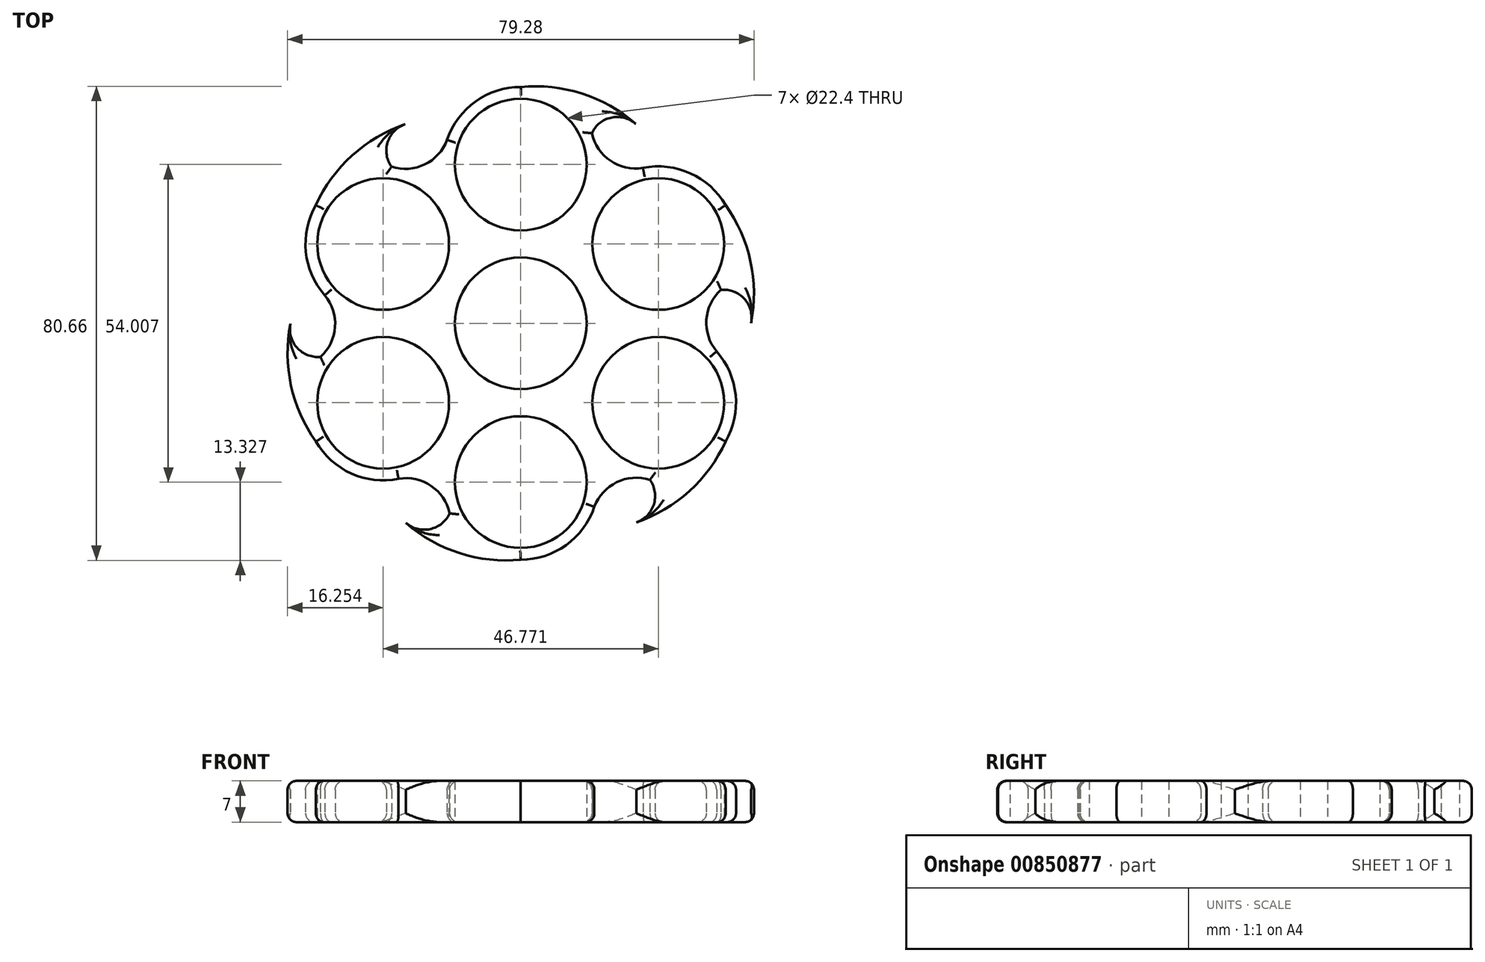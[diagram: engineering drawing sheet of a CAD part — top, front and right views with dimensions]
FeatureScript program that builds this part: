
annotation { "Feature Type Name" : "Feature", "Feature Type Description" : "" }
export const myFeature = defineFeature(function(context is Context, id is Id, definition is map)
    precondition{}
    {
        {
            var Q0;
            Q0=qCreatedBy(makeId("Top.planeOp"),FACE);
            var sketch = newSketch(context, id + "F0", { "sketchPlane" : qUnion([Q0])});
            skCircle(sketch, "E0", {"center": v(0, 0) * mm, "radius": 11.2 * mm});
            skCircle(sketch, "E1", {"center": v(0, 27) * mm, "radius": 11.2 * mm});
            skArc(sketch, "E2", {"start": v(12.73, 30.5) * mm, "mid": v(12.44, 31.42) * mm, "end": v(12.08, 32.33) * mm});
            skArc(sketch, "E3.1.0", {"start": v(-20.05, 26.27) * mm, "mid": v(-21, 26.48) * mm, "end": v(-21.96, 26.62) * mm});
            skCircle(sketch, "E3.1.1", {"center": v(-23.39, 13.5) * mm, "radius": 11.2 * mm});
            skArc(sketch, "E3.2.0", {"start": v(-32.78, -4.22) * mm, "mid": v(-33.43, -4.94) * mm, "end": v(-34.04, -5.7) * mm});
            skCircle(sketch, "E3.2.1", {"center": v(-23.39, -13.5) * mm, "radius": 11.2 * mm});
            skArc(sketch, "E3.3.0", {"start": v(-12.73, -30.5) * mm, "mid": v(-12.44, -31.42) * mm, "end": v(-12.08, -32.33) * mm});
            skCircle(sketch, "E3.3.1", {"center": v(0, -27) * mm, "radius": 11.2 * mm});
            skArc(sketch, "E3.4.0", {"start": v(20.05, -26.27) * mm, "mid": v(21, -26.48) * mm, "end": v(21.96, -26.62) * mm});
            skCircle(sketch, "E3.4.1", {"center": v(23.39, -13.5) * mm, "radius": 11.2 * mm});
            skArc(sketch, "E3.5.0", {"start": v(32.78, 4.22) * mm, "mid": v(33.43, 4.94) * mm, "end": v(34.04, 5.7) * mm});
            skCircle(sketch, "E3.5.1", {"center": v(23.39, 13.5) * mm, "radius": 11.2 * mm});
            skArc(sketch, "E4", {"start": v(12.08, 32.33) * mm, "mid": v(15.25, 27.64) * mm, "end": v(20.77, 26.44) * mm});
            skArc(sketch, "E5.1.0", {"start": v(-21.96, 26.62) * mm, "mid": v(-16.32, 27.02) * mm, "end": v(-12.51, 31.21) * mm});
            skArc(sketch, "E5.2.0", {"start": v(-34.04, -5.7) * mm, "mid": v(-31.56, -0.62) * mm, "end": v(-33.29, 4.77) * mm});
            skArc(sketch, "E5.3.0", {"start": v(-12.08, -32.33) * mm, "mid": v(-15.25, -27.64) * mm, "end": v(-20.77, -26.44) * mm});
            skArc(sketch, "E5.4.0", {"start": v(21.96, -26.62) * mm, "mid": v(16.32, -27.02) * mm, "end": v(12.51, -31.21) * mm});
            skArc(sketch, "E5.5.0", {"start": v(34.04, 5.7) * mm, "mid": v(31.56, 0.62) * mm, "end": v(33.29, -4.77) * mm});
            skArc(sketch, "E6", {"start": v(19.5, 33.94) * mm, "mid": v(10.4, 39.09) * mm, "end": v(0, 40.2) * mm});
            skArc(sketch, "E7", {"start": v(19.5, 33.94) * mm, "mid": v(15.4, 35) * mm, "end": v(12.08, 32.33) * mm});
            skArc(sketch, "E8.1.0", {"start": v(-19.64, 33.87) * mm, "mid": v(-28.65, 28.55) * mm, "end": v(-34.82, 20.1) * mm});
            skArc(sketch, "E8.1.1", {"start": v(-19.64, 33.87) * mm, "mid": v(-22.61, 30.83) * mm, "end": v(-21.96, 26.62) * mm});
            skArc(sketch, "E8.2.0", {"start": v(-39.15, -0.07) * mm, "mid": v(-39.05, -10.54) * mm, "end": v(-34.82, -20.1) * mm});
            skArc(sketch, "E8.2.1", {"start": v(-39.15, -0.07) * mm, "mid": v(-38, -4.17) * mm, "end": v(-34.04, -5.7) * mm});
            skArc(sketch, "E8.3.0", {"start": v(-19.5, -33.94) * mm, "mid": v(-10.4, -39.09) * mm, "end": v(0, -40.2) * mm});
            skArc(sketch, "E8.3.1", {"start": v(-19.5, -33.94) * mm, "mid": v(-15.4, -35) * mm, "end": v(-12.08, -32.33) * mm});
            skArc(sketch, "E8.4.0", {"start": v(19.64, -33.87) * mm, "mid": v(28.65, -28.55) * mm, "end": v(34.82, -20.1) * mm});
            skArc(sketch, "E8.4.1", {"start": v(19.64, -33.87) * mm, "mid": v(22.61, -30.83) * mm, "end": v(21.96, -26.62) * mm});
            skArc(sketch, "E8.5.0", {"start": v(39.15, 0.07) * mm, "mid": v(39.05, 10.54) * mm, "end": v(34.82, 20.1) * mm});
            skArc(sketch, "E8.5.1", {"start": v(39.15, 0.07) * mm, "mid": v(38, 4.17) * mm, "end": v(34.04, 5.7) * mm});
            skArc(sketch, "E9.trimOffspring", {"start": v(0, 40.2) * mm, "mid": v(-7.7, 37.72) * mm, "end": v(-12.51, 31.21) * mm});
            skArc(sketch, "E10.trimOffspring", {"start": v(34.82, 20.1) * mm, "mid": v(28.82, 25.53) * mm, "end": v(20.77, 26.44) * mm});
            skArc(sketch, "E11.trimOffspring", {"start": v(34.82, -20.1) * mm, "mid": v(36.52, -12.19) * mm, "end": v(33.29, -4.77) * mm});
            skArc(sketch, "E12.trimOffspring", {"start": v(0, -40.2) * mm, "mid": v(7.7, -37.72) * mm, "end": v(12.51, -31.21) * mm});
            skArc(sketch, "E13.trimOffspring", {"start": v(-34.82, -20.1) * mm, "mid": v(-28.82, -25.53) * mm, "end": v(-20.77, -26.44) * mm});
            skArc(sketch, "E14.trimOffspring", {"start": v(-34.82, 20.1) * mm, "mid": v(-36.52, 12.19) * mm, "end": v(-33.29, 4.77) * mm});
            skSolve(sketch);
        }
        {
            var Q0;
            Q0=makeQuery(id+"F0.imprint","IMPRINT",FACE,{"disambiguationData":[TD([[makeQuery(id+"F0.imprint","IMPRINT",EDGE,{"derivedFrom":sQuery(id+"F0.wireOp",EDGE,"E0")}),-1.0]])]});
            extrude(context, id + "F1", {"entities" : qUnion([Q0]), "depth" : 7 * mm, "offsetDistance" : 25 * mm});
        }
        {
            var Q0;
            Q0=makeQuery(id+"F1.opExtrude","CAP_EDGE",EDGE,{"disambiguationData":[OSD([sQuery(id+"F0.wireOp",EDGE,"E8.2.0")])],"isStart":false});
            var Q1;
            Q1=makeQuery(id+"F1.opExtrude","CAP_EDGE",EDGE,{"disambiguationData":[OSD([sQuery(id+"F0.wireOp",EDGE,"E5.2.0")])],"isStart":false});
            var Q2;
            Q2=makeQuery(id+"F1.opExtrude","CAP_EDGE",EDGE,{"disambiguationData":[OSD([sQuery(id+"F0.wireOp",EDGE,"E8.2.1")])],"isStart":false});
            var Q3;
            Q3=makeQuery(id+"F1.opExtrude","CAP_EDGE",EDGE,{"disambiguationData":[OSD([sQuery(id+"F0.wireOp",EDGE,"E14.trimOffspring")])],"isStart":false});
            var Q4;
            Q4=makeQuery(id+"F1.opExtrude","CAP_EDGE",EDGE,{"disambiguationData":[OSD([sQuery(id+"F0.wireOp",EDGE,"E8.1.0")])],"isStart":false});
            var Q5;
            Q5=makeQuery(id+"F1.opExtrude","CAP_EDGE",EDGE,{"disambiguationData":[OSD([sQuery(id+"F0.wireOp",EDGE,"E8.1.1")])],"isStart":false});
            var Q6;
            Q6=makeQuery(id+"F1.opExtrude","CAP_EDGE",EDGE,{"disambiguationData":[OSD([sQuery(id+"F0.wireOp",EDGE,"E5.1.0")])],"isStart":false});
            var Q7;
            Q7=makeQuery(id+"F1.opExtrude","CAP_EDGE",EDGE,{"disambiguationData":[OSD([sQuery(id+"F0.wireOp",EDGE,"E9.trimOffspring")])],"isStart":false});
            var Q8;
            Q8=makeQuery(id+"F1.opExtrude","CAP_EDGE",EDGE,{"disambiguationData":[OSD([sQuery(id+"F0.wireOp",EDGE,"E6")])],"isStart":false});
            var Q9;
            Q9=makeQuery(id+"F1.opExtrude","CAP_EDGE",EDGE,{"disambiguationData":[OSD([sQuery(id+"F0.wireOp",EDGE,"E7")])],"isStart":false});
            var Q10;
            Q10=makeQuery(id+"F1.opExtrude","CAP_EDGE",EDGE,{"disambiguationData":[OSD([sQuery(id+"F0.wireOp",EDGE,"E4")])],"isStart":false});
            var Q11;
            Q11=makeQuery(id+"F1.opExtrude","CAP_EDGE",EDGE,{"disambiguationData":[OSD([sQuery(id+"F0.wireOp",EDGE,"E10.trimOffspring")])],"isStart":false});
            var Q12;
            Q12=makeQuery(id+"F1.opExtrude","CAP_EDGE",EDGE,{"disambiguationData":[OSD([sQuery(id+"F0.wireOp",EDGE,"E8.5.0")])],"isStart":false});
            var Q13;
            Q13=makeQuery(id+"F1.opExtrude","CAP_EDGE",EDGE,{"disambiguationData":[OSD([sQuery(id+"F0.wireOp",EDGE,"E8.5.1")])],"isStart":false});
            var Q14;
            Q14=makeQuery(id+"F1.opExtrude","CAP_EDGE",EDGE,{"disambiguationData":[OSD([sQuery(id+"F0.wireOp",EDGE,"E5.5.0")])],"isStart":false});
            var Q15;
            Q15=makeQuery(id+"F1.opExtrude","CAP_EDGE",EDGE,{"disambiguationData":[OSD([sQuery(id+"F0.wireOp",EDGE,"E11.trimOffspring")])],"isStart":false});
            var Q16;
            Q16=makeQuery(id+"F1.opExtrude","CAP_EDGE",EDGE,{"disambiguationData":[OSD([sQuery(id+"F0.wireOp",EDGE,"E8.4.0")])],"isStart":false});
            var Q17;
            Q17=makeQuery(id+"F1.opExtrude","CAP_EDGE",EDGE,{"disambiguationData":[OSD([sQuery(id+"F0.wireOp",EDGE,"E8.4.1")])],"isStart":false});
            var Q18;
            Q18=makeQuery(id+"F1.opExtrude","CAP_EDGE",EDGE,{"disambiguationData":[OSD([sQuery(id+"F0.wireOp",EDGE,"E5.4.0")])],"isStart":false});
            var Q19;
            Q19=makeQuery(id+"F1.opExtrude","CAP_EDGE",EDGE,{"disambiguationData":[OSD([sQuery(id+"F0.wireOp",EDGE,"E12.trimOffspring")])],"isStart":false});
            var Q20;
            Q20=makeQuery(id+"F1.opExtrude","CAP_EDGE",EDGE,{"disambiguationData":[OSD([sQuery(id+"F0.wireOp",EDGE,"E8.3.0")])],"isStart":false});
            var Q21;
            Q21=makeQuery(id+"F1.opExtrude","CAP_EDGE",EDGE,{"disambiguationData":[OSD([sQuery(id+"F0.wireOp",EDGE,"E8.3.1")])],"isStart":false});
            var Q22;
            Q22=makeQuery(id+"F1.opExtrude","CAP_EDGE",EDGE,{"disambiguationData":[OSD([sQuery(id+"F0.wireOp",EDGE,"E5.3.0")])],"isStart":false});
            var Q23;
            Q23=makeQuery(id+"F1.opExtrude","CAP_EDGE",EDGE,{"disambiguationData":[OSD([sQuery(id+"F0.wireOp",EDGE,"E13.trimOffspring")])],"isStart":false});
            fillet(context, id + "F2", {"entities" : qUnion([Q0, Q1, Q2, Q3, Q4, Q5, Q6, Q7, Q8, Q9, Q10, Q11, Q12, Q13, Q14, Q15, Q16, Q17, Q18, Q19, Q20, Q21, Q22, Q23]), "radius" : 1.5 * mm, "tangentPropagation" : true, "allowEdgeOverflow" : false});
        }
        {
            var Q0;
            Q0=makeQuery(id+"F1.opExtrude","CAP_EDGE",EDGE,{"disambiguationData":[OSD([sQuery(id+"F0.wireOp",EDGE,"E12.trimOffspring")])],"isStart":true});
            var Q1;
            Q1=makeQuery(id+"F1.opExtrude","CAP_EDGE",EDGE,{"disambiguationData":[OSD([sQuery(id+"F0.wireOp",EDGE,"E8.3.0")])],"isStart":true});
            var Q2;
            Q2=makeQuery(id+"F1.opExtrude","CAP_EDGE",EDGE,{"disambiguationData":[OSD([sQuery(id+"F0.wireOp",EDGE,"E14.trimOffspring")])],"isStart":true});
            var Q3;
            Q3=makeQuery(id+"F1.opExtrude","CAP_EDGE",EDGE,{"disambiguationData":[OSD([sQuery(id+"F0.wireOp",EDGE,"E8.1.1")])],"isStart":true});
            var Q4;
            Q4=makeQuery(id+"F1.opExtrude","CAP_EDGE",EDGE,{"disambiguationData":[OSD([sQuery(id+"F0.wireOp",EDGE,"E5.1.0")])],"isStart":true});
            var Q5;
            Q5=makeQuery(id+"F1.opExtrude","CAP_EDGE",EDGE,{"disambiguationData":[OSD([sQuery(id+"F0.wireOp",EDGE,"E9.trimOffspring")])],"isStart":true});
            var Q6;
            Q6=makeQuery(id+"F1.opExtrude","CAP_EDGE",EDGE,{"disambiguationData":[OSD([sQuery(id+"F0.wireOp",EDGE,"E6")])],"isStart":true});
            var Q7;
            Q7=makeQuery(id+"F1.opExtrude","CAP_EDGE",EDGE,{"disambiguationData":[OSD([sQuery(id+"F0.wireOp",EDGE,"E7")])],"isStart":true});
            var Q8;
            Q8=makeQuery(id+"F1.opExtrude","CAP_EDGE",EDGE,{"disambiguationData":[OSD([sQuery(id+"F0.wireOp",EDGE,"E4")])],"isStart":true});
            var Q9;
            Q9=makeQuery(id+"F1.opExtrude","CAP_EDGE",EDGE,{"disambiguationData":[OSD([sQuery(id+"F0.wireOp",EDGE,"E10.trimOffspring")])],"isStart":true});
            var Q10;
            Q10=makeQuery(id+"F1.opExtrude","CAP_EDGE",EDGE,{"disambiguationData":[OSD([sQuery(id+"F0.wireOp",EDGE,"E8.5.0")])],"isStart":true});
            var Q11;
            Q11=makeQuery(id+"F1.opExtrude","CAP_EDGE",EDGE,{"disambiguationData":[OSD([sQuery(id+"F0.wireOp",EDGE,"E8.5.1")])],"isStart":true});
            var Q12;
            Q12=makeQuery(id+"F1.opExtrude","CAP_EDGE",EDGE,{"disambiguationData":[OSD([sQuery(id+"F0.wireOp",EDGE,"E5.5.0")])],"isStart":true});
            var Q13;
            Q13=makeQuery(id+"F1.opExtrude","CAP_EDGE",EDGE,{"disambiguationData":[OSD([sQuery(id+"F0.wireOp",EDGE,"E11.trimOffspring")])],"isStart":true});
            var Q14;
            Q14=makeQuery(id+"F1.opExtrude","CAP_EDGE",EDGE,{"disambiguationData":[OSD([sQuery(id+"F0.wireOp",EDGE,"E8.4.0")])],"isStart":true});
            var Q15;
            Q15=makeQuery(id+"F1.opExtrude","CAP_EDGE",EDGE,{"disambiguationData":[OSD([sQuery(id+"F0.wireOp",EDGE,"E8.4.1")])],"isStart":true});
            var Q16;
            Q16=makeQuery(id+"F1.opExtrude","CAP_EDGE",EDGE,{"disambiguationData":[OSD([sQuery(id+"F0.wireOp",EDGE,"E5.3.0")])],"isStart":true});
            var Q17;
            Q17=makeQuery(id+"F1.opExtrude","CAP_EDGE",EDGE,{"disambiguationData":[OSD([sQuery(id+"F0.wireOp",EDGE,"E13.trimOffspring")])],"isStart":true});
            var Q18;
            Q18=makeQuery(id+"F1.opExtrude","CAP_EDGE",EDGE,{"disambiguationData":[OSD([sQuery(id+"F0.wireOp",EDGE,"E8.2.0")])],"isStart":true});
            var Q19;
            Q19=makeQuery(id+"F1.opExtrude","CAP_EDGE",EDGE,{"disambiguationData":[OSD([sQuery(id+"F0.wireOp",EDGE,"E8.1.0")])],"isStart":true});
            var Q20;
            Q20=makeQuery(id+"F1.opExtrude","CAP_EDGE",EDGE,{"disambiguationData":[OSD([sQuery(id+"F0.wireOp",EDGE,"E8.3.1")])],"isStart":true});
            var Q21;
            Q21=makeQuery(id+"F1.opExtrude","CAP_EDGE",EDGE,{"disambiguationData":[OSD([sQuery(id+"F0.wireOp",EDGE,"E8.2.1")])],"isStart":true});
            fillet(context, id + "F3", {"entities" : qUnion([Q0, Q1, Q2, Q3, Q4, Q5, Q6, Q7, Q8, Q9, Q10, Q11, Q12, Q13, Q14, Q15, Q16, Q17, Q18, Q19, Q20, Q21]), "radius" : 1.5 * mm, "tangentPropagation" : true, "allowEdgeOverflow" : false});
        }
    });
